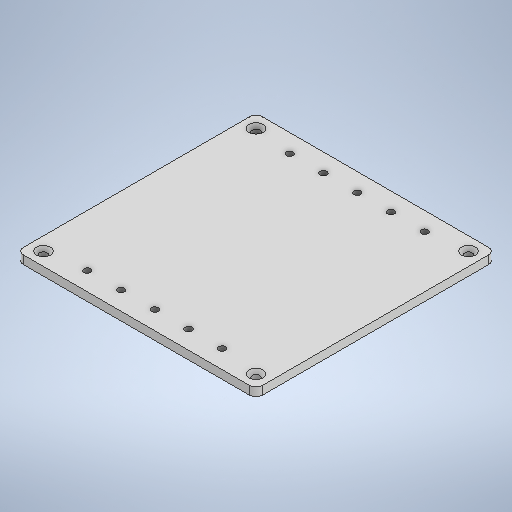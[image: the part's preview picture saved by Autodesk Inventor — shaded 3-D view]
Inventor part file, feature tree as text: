
AUTODESK INVENTOR PART (.ipt)
format: ipt  version: 2025 (Build 290162000, 162)  size: 274,432 bytes
history: native  units: mm
features: sketch x3, hole x2, extrude x1, fillet x1
ambient origin geometry x8: Origin, YZ Plane, XZ Plane, XY Plane, X Axis, Y Axis, Z Axis, Center Point
bodies: Solid1 (feature_tree)
feature tree (7):
  extrude  "Extrusion1"  Depth=180.0mm
  hole  "Hole1"  [1 undecoded]
  hole  "Hole2"  [1 undecoded]
  fillet  "Fillet1"  Radius=80.0mm
  sketch  "Sketch1"  dims[d0=180.0mm d1=180.0mm]
  sketch  "Sketch2"  dims[d2=6.35mm d3=0.0mm d4=160.0mm]
  sketch  "Sketch3"  dims[d5=80.0mm d6=160.0mm d7=80.0mm d8=5.5mm d9=6.0mm d10=10.4mm d11=2.0mm d12=90.0deg d13=8.0mm d14=20.594885mm d15=152.4mm d16=50.8mm d17=76.2mm d18=25.4mm d19=4.9784mm d20=12.7mm d21=12.878mm d22=2.0mm d23=14.3117mm d24=8.0mm d25=20.594885mm d26=5.0mm d27=25.4mm d28=25.4mm]
note: 2 required parameter values undecoded (feature->parameter linkage not recoverable at this tier; creation-order binding heuristic only, values carry confidence <= 0.55)
